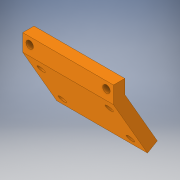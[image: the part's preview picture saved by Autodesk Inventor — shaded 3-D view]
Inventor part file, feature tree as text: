
AUTODESK INVENTOR PART (.ipt)
format: ipt  version: 2019 (Build 230136000, 136)  size: 137,216 bytes
history: native  units: in
note: dims shown in document units (in); Inventor stores cm internally (conversion verified against a paired STEP export)
features: sketch x4, extrude x2, hole x2, plane x1, projected_geometry x1
ambient origin geometry x8: Origin, YZ Plane, XZ Plane, XY Plane, X Axis, Y Axis, Z Axis, Center Point
bodies: Solid1 (feature_tree)
feature tree (10):
  extrude  "Extrusion1"  Depth=0.25in
  plane  "Work Plane1"
  extrude  "Extrusion2"  TaperAngle=30.0deg  [1 undecoded]
  hole  "Hole1"  [1 undecoded]
  hole  "Hole2"  [1 undecoded]
  sketch  "Sketch1"  dims[d0=0.375in d1=0.25in]
  sketch  "Sketch2"  dims[d2=2.0in d3=0.0in d4=30.0deg]
  sketch  "Sketch3"  dims[d5=0.25in d6=1.5in d7=0.0in]
  sketch  "Sketch4"  dims[d8=0.154in d9=0.308in d10=0.154in d11=0.154in d12=0.154in d13=0.165in d14=0.75in d15=0.375in d16=0.25in d17=0.5635in d18=1.0in d19=0.8108in d20=0.25in d21=0.25in d22=0.25in d23=0.25in d24=0.25in d25=0.25in d26=0.25in d27=0.25in d28=0.165in d29=0.75in d30=0.375in d31=0.25in d32=0.5635in d33=1.0in d34=0.8108in]
  projected_geometry  "Projected Loop1"
note: 3 required parameter values undecoded (feature->parameter linkage not recoverable at this tier; creation-order binding heuristic only, values carry confidence <= 0.55)
